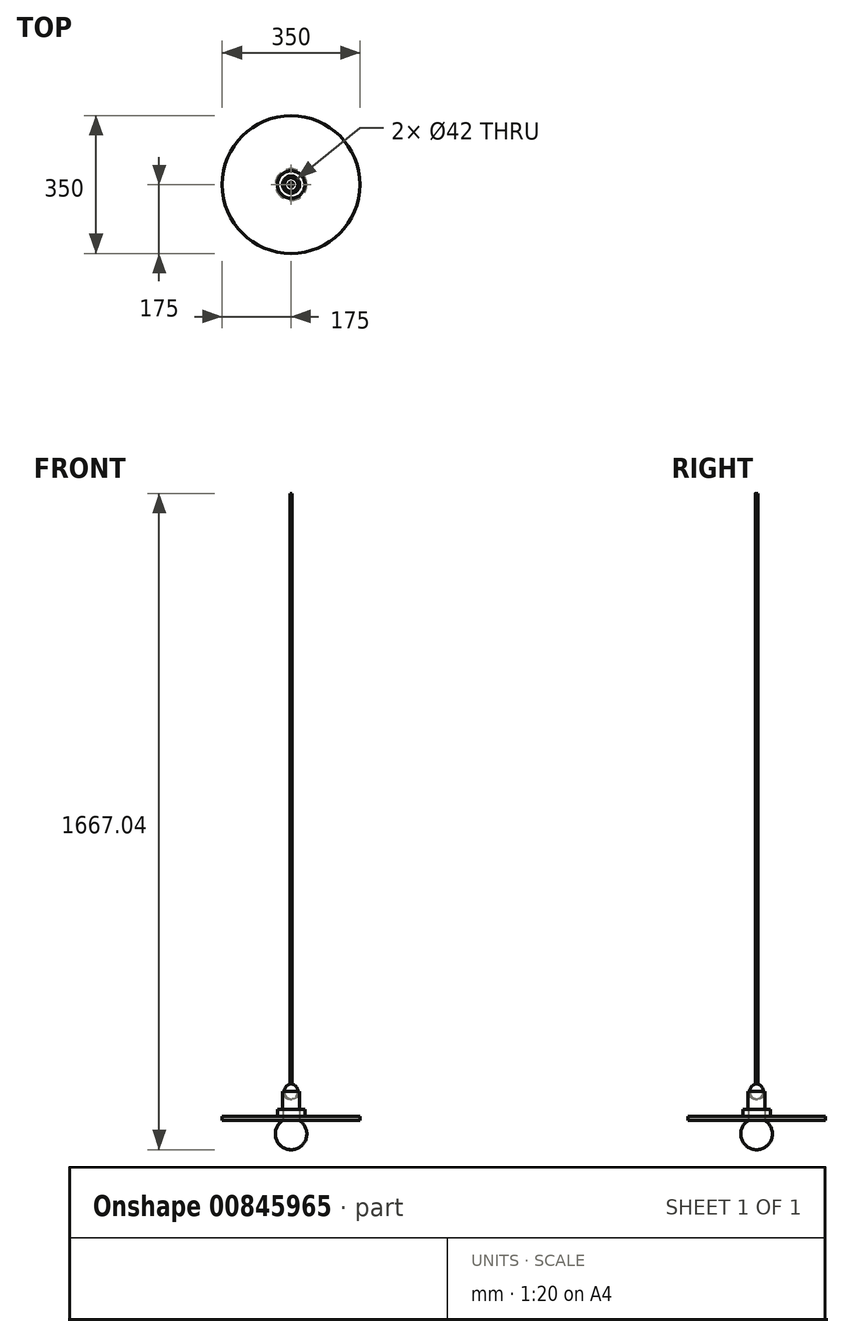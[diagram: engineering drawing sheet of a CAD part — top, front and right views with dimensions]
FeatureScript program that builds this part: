
annotation { "Feature Type Name" : "Feature", "Feature Type Description" : "" }
export const myFeature = defineFeature(function(context is Context, id is Id, definition is map)
    precondition{}
    {
        {
            var Q0;
            Q0=qCreatedBy(makeId("Top.planeOp"),FACE);
            var sketch = newSketch(context, id + "F0", { "sketchPlane" : qUnion([Q0])});
            skCircle(sketch, "E0", {"center": v(0, 0) * mm, "radius": 175 * mm});
            skCircle(sketch, "E1", {"center": v(0, 0) * mm, "radius": 21 * mm});
            skSolve(sketch);
        }
        {
            var Q0;
            Q0 = qSketchRegion(id + "F0", true);
            extrude(context, id + "F1", {"entities" : qUnion([Q0]), "depth" : 10 * mm, "offsetDistance" : 25.4 * mm});
        }
        {
            var Q0;
            Q0=makeQuery(id+"F1.opExtrude","CAP_FACE",FACE,{"disambiguationData":[OSD([sQuery(id+"F0.wireOp",EDGE,"E0"),sQuery(id+"F0.wireOp",EDGE,"E1")])],"isStart":false});
            var sketch = newSketch(context, id + "F2", { "sketchPlane" : qUnion([Q0])});
            skCircle(sketch, "E2", {"center": v(0, 0) * mm, "radius": 21 * mm});
            skCircle(sketch, "E3", {"center": v(0, 0) * mm, "radius": 35 * mm});
            skSolve(sketch);
        }
        {
            var Q0;
            Q0 = qSketchRegion(id + "F2", true);
            extrude(context, id + "F3", {"entities" : qUnion([Q0]), "depth" : 18 * mm, "offsetDistance" : 25 * mm});
        }
        {
            var Q0;
            Q0=qCreatedBy(makeId("Front.planeOp"),FACE);
            var sketch = newSketch(context, id + "F4", { "sketchPlane" : qUnion([Q0])});
            skLineSegment(sketch, "E4", {"start": v(0, 28) * mm, "end": v(0, 93) * mm});
            skLineSegment(sketch, "E5", {"start": v(0, 93) * mm, "end": v(-6.32, 93) * mm});
            skLineSegment(sketch, "E6", {"start": v(0, 28) * mm, "end": v(-21.82, 28) * mm});
            skLineSegment(sketch, "E7", {"start": v(-21.82, 28) * mm, "end": v(-21.82, 73.9) * mm});
            skArc(sketch, "E8", {"start": v(-6.32, 93) * mm, "mid": v(-17.45, 86.2) * mm, "end": v(-21.82, 73.9) * mm});
            skSolve(sketch);
        }
        {
            var Q0;
            Q0 = qSketchRegion(id + "F4", true);
            var Q1;
            Q1=sQuery(id+"F4.wireOp",EDGE,"E4");
            revolve(context, id + "F5", {"surfaceOperationType" : NewSurfaceOperationType.NEW, "entities" : qUnion([Q0]), "axis" : qUnion([Q1]), "revolveType" : RevolveType.FULL});
        }
        {
            var Q0;
            Q0=qCreatedBy(makeId("Front.planeOp"),FACE);
            var sketch = newSketch(context, id + "F6", { "sketchPlane" : qUnion([Q0])});
            skArc(sketch, "E9", {"start": v(-21, 0) * mm, "mid": v(-38.48, -44.96) * mm, "end": v(0, -74.04) * mm});
            skLineSegment(sketch, "E10", {"start": v(0, 0) * mm, "end": v(-21, 0) * mm});
            skLineSegment(sketch, "E11", {"start": v(0, 0) * mm, "end": v(0, -74.04) * mm});
            skSolve(sketch);
        }
        {
            var Q0;
            Q0 = qSketchRegion(id + "F6", true);
            var Q1;
            Q1=sQuery(id+"F6.wireOp",EDGE,"E11");
            revolve(context, id + "F7", {"surfaceOperationType" : NewSurfaceOperationType.NEW, "entities" : qUnion([Q0]), "axis" : qUnion([Q1]), "revolveType" : RevolveType.FULL});
        }
        {
            var Q0;
            Q0=makeQuery(id+"F5.opRevolve","SWEPT_FACE",FACE,{"disambiguationData":[OSD([sQuery(id+"F4.wireOp",EDGE,"E5")])]});
            var sketch = newSketch(context, id + "F8", { "sketchPlane" : qUnion([Q0])});
            skCircle(sketch, "E12", {"center": v(0, 0) * mm, "radius": 3 * mm});
            skSolve(sketch);
        }
        {
            var Q0;
            Q0 = qSketchRegion(id + "F8", true);
            extrude(context, id + "F9", {"entities" : qUnion([Q0]), "depth" : 1500 * mm, "offsetDistance" : 25 * mm});
        }
    });
